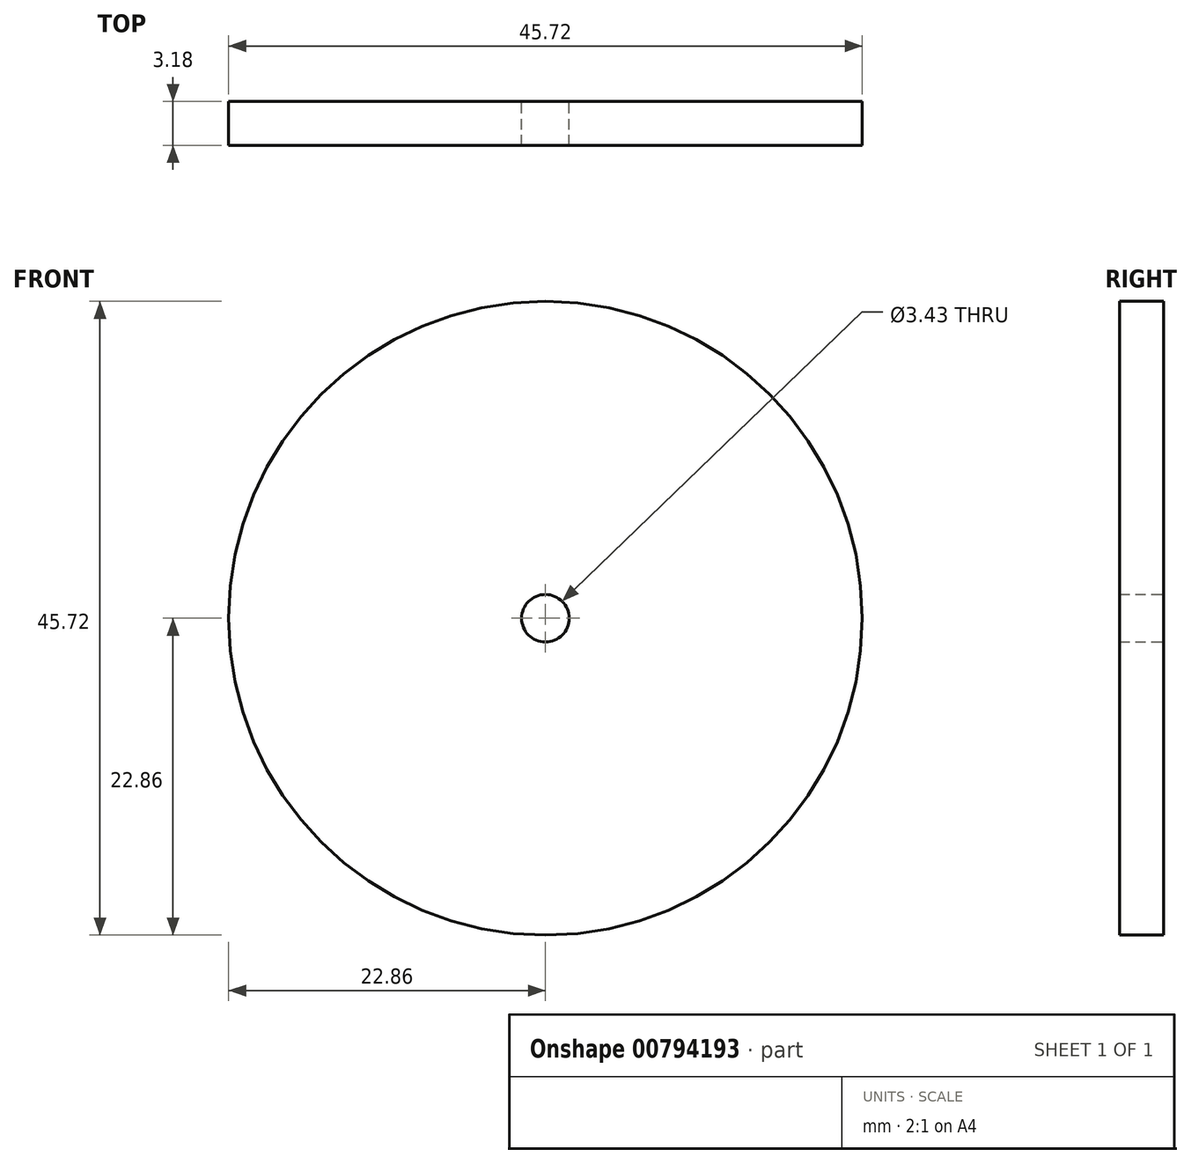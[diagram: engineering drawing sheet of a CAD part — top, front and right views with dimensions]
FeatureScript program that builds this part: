
annotation { "Feature Type Name" : "Feature", "Feature Type Description" : "" }
export const myFeature = defineFeature(function(context is Context, id is Id, definition is map)
    precondition{}
    {
        {
            var Q0;
            Q0=qCreatedBy(makeId("Front.planeOp"),FACE);
            var sketch = newSketch(context, id + "F0", { "sketchPlane" : qUnion([Q0])});
            skCircle(sketch, "E0", {"center": v(0, 0) * mm, "radius": 22.86 * mm});
            skCircle(sketch, "E1", {"center": v(0, 0) * mm, "radius": 1.71 * mm});
            skSolve(sketch);
        }
        {
            var Q0;
            Q0=makeQuery(id+"F0.imprint","IMPRINT",FACE,{"disambiguationData":[TD([[makeQuery(id+"F0.imprint","IMPRINT",EDGE,{"derivedFrom":sQuery(id+"F0.wireOp",EDGE,"E0")}),1.0]])]});
            extrude(context, id + "F1", {"entities" : qUnion([Q0]), "depth" : 3.17 * mm, "offsetDistance" : 25.4 * mm});
        }
    });
